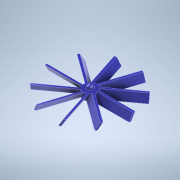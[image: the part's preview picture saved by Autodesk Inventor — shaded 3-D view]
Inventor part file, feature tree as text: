
AUTODESK INVENTOR PART (.ipt)
format: ipt  version: 2021 (Build 250183000, 183)  size: 166,400 bytes
history: native  units: mm
features: extrude x4, sketch x4, pattern_circular x1, fillet x1
ambient origin geometry x8: Origin, YZ Plane, XZ Plane, XY Plane, X Axis, Y Axis, Z Axis, Center Point
bodies: Solid1 (feature_tree)
feature tree (10):
  extrude  "Extrusion1"  Depth=10.0mm TaperAngle=0.0deg
  extrude  "Extrusion2"  Depth=10.0mm
  pattern_circular  "Circular Pattern1"  [2 undecoded]
  extrude  "Extrusion3"  Depth=2.0mm TaperAngle=0.0deg
  fillet  "Fillet1"  Radius=100.0mm
  extrude  "Extrusion4"  Depth=10.0mm
  sketch  "Sketch1"  dims[d0=20.0mm d1=10.0mm d2=0.0mm]
  sketch  "Sketch3"  dims[d3=3.0mm d4=10.0mm]
  sketch  "Sketch4"  dims[d5=10.0mm]
  sketch  "Sketch5"  dims[d6=60.0deg d7=5.0mm d8=63.5mm d9=0.0mm d10=100.0mm d11=360.0deg d13=10.0mm d14=5.0mm d15=0.0mm d16=5.0mm d17=5.0mm d18=2.0mm d19=0.0mm]
note: 2 required parameter values undecoded (feature->parameter linkage not recoverable at this tier; creation-order binding heuristic only, values carry confidence <= 0.55)
